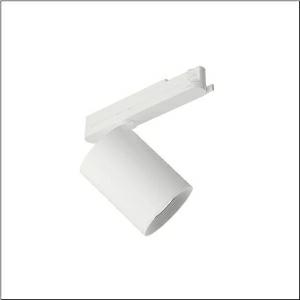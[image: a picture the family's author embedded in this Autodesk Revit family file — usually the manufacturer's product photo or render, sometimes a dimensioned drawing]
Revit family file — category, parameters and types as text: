
# Revit family: spot_21_51se14mba5b
name_source: partatom
category: Lighting Fixtures
units: mm (PartAtom-declared; Revit-internal decimal feet)

## family parameters
Cut with Voids When Loaded = No
Host = Face
Light Source = No
Part Type = Normal
Room Calculation Point = No
Round Connector Dimension = Use Diameter
Shared = No

## types (1)
- --- (1 x LED, 5340 lm, 41.8 W, 2700K)
    Apparent Load = 42 VA
    CIE Flux Codes = 96 99 100 100 100
    Color Rendering = 90
    Color Temperature = 2700K
    Default Elevation = 1800 mm
    Description = Spot 21, directional spotlight, light control with lens, of PMMA, LED rated luminous flux: 5.030lm, light colour: 927, control gear: ECG Multilumen, with 3-phase adapter, mains connection: 220..240V, AC, 50/60Hz, of aluminium, traffic white (RAL 9016), length: 213mm, diameter: 105mm, protection rating (complete): IP20, insulation class (complete): insulation class I (protective earthing), certification: CE, impact resistance: IK02, permissible ambient temperature for indoor applications: -20..+40°C, packaging unit: 1 piece
    Height = 175 mm
    Lamp = 1 x LED
    Lamp Light Flux = 5340 lm
    Lamp Power = 41.8 W
    Lamp count = 1
    Length = 105 mm
    Luminous efficacy = 128 lm/W
    Manufacturer = Siteco
    ModVariant = No
    Model = 51SE14MBA5B
    Mounting Place = Ceiling
    Mounting Type = Pendant
    Number of Poles = 1
    OnlyDefault = Yes
    Power Factor = 1
    Product Name = Spot 21
    Product group = directional spotlight
    ProductGroupID = 904
    Protection Class = Protection class I
    Protection Degree = IP 20
    RLX_Detail_Level = 1
    RlxData = <blob elided: 17633 chars, md5=8e3f0e5d>
    Socket = socket
    Standby Power = 0 W
    System Light Flux = 5340 lm
    System Power = 42 W
    Type Comments = factory setting: luminous flux: 100 % | (ON | ON | ON | ON) | 1050 mA
    Type Image = l_1003976.jpg
    URL = http://relux.com
    VarID = @adj_052637
    Voltage = 0 V
    Weight = 0.00 kg
    Width = 0 mm  [stored 0 ft]

note: [stored X ft] marks values corroborated as IEEE doubles in the binary element streams (Revit-internal decimal feet)

## geometry (parser evidence)
native form markers: Blend x4, Sweep x9
no freeform markers — native parametric forms only
